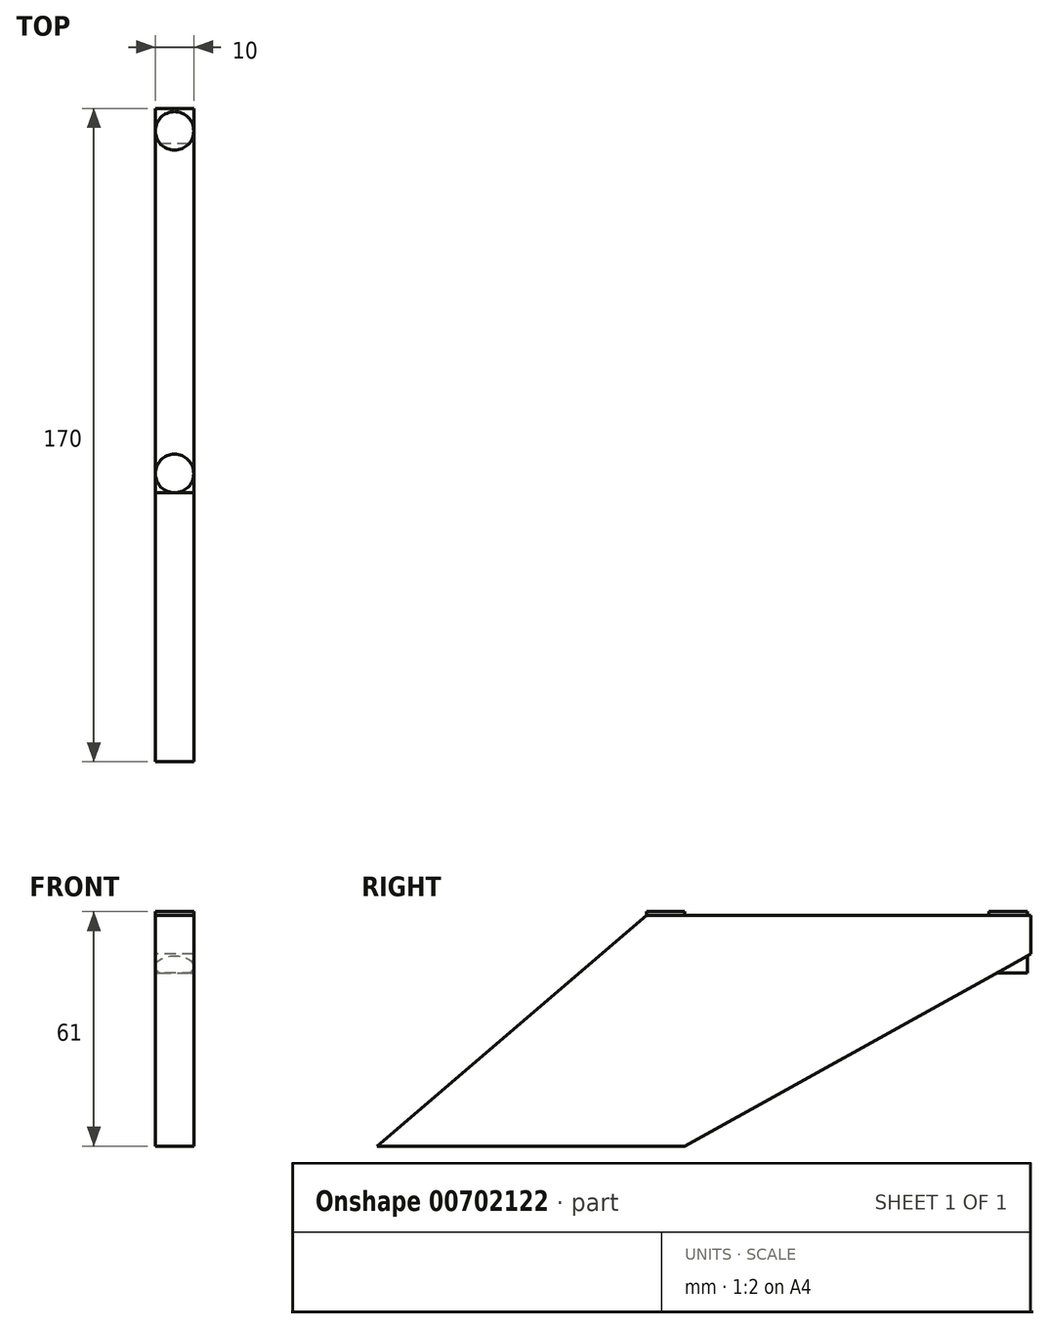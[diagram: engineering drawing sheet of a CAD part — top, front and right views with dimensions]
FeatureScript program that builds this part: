
annotation { "Feature Type Name" : "Feature", "Feature Type Description" : "" }
export const myFeature = defineFeature(function(context is Context, id is Id, definition is map)
    precondition{}
    {
        {
            var Q0;
            Q0=qCreatedBy(makeId("Right.planeOp"),FACE);
            var sketch = newSketch(context, id + "F0", { "sketchPlane" : qUnion([Q0])});
            skLineSegment(sketch, "E0", {"start": v(-41.23, -36.86) * mm, "end": v(-41.23, 23.14) * mm});
            skLineSegment(sketch, "E1", {"start": v(-41.23, 23.14) * mm, "end": v(58.77, 23.14) * mm});
            skLineSegment(sketch, "E2", {"start": v(-41.23, -36.86) * mm, "end": v(-111.23, -36.86) * mm});
            skLineSegment(sketch, "E3", {"start": v(-111.23, -36.86) * mm, "end": v(-41.23, 23.14) * mm});
            skLineSegment(sketch, "E4", {"start": v(58.77, 23.14) * mm, "end": v(58.77, 13.14) * mm});
            skLineSegment(sketch, "E5", {"start": v(58.77, 13.14) * mm, "end": v(-31.23, -36.86) * mm});
            skLineSegment(sketch, "E6", {"start": v(-31.23, -36.86) * mm, "end": v(-41.23, -36.86) * mm});
            skSolve(sketch);
        }
        {
            var Q0;
            Q0=makeQuery(id+"F0.imprint","IMPRINT",FACE,{"disambiguationData":[TD([[makeQuery(id+"F0.imprint","IMPRINT",EDGE,{"derivedFrom":sQuery(id+"F0.wireOp",EDGE,"E0")}),1.0]])]});
            var Q1;
            Q1=makeQuery(id+"F0.imprint","IMPRINT",FACE,{"disambiguationData":[TD([[makeQuery(id+"F0.imprint","IMPRINT",EDGE,{"derivedFrom":sQuery(id+"F0.wireOp",EDGE,"E0")}),-1.0]])]});
            extrude(context, id + "F1", {"entities" : qUnion([Q0, Q1]), "endBound" : BoundingType.SYMMETRIC, "depth" : 10 * mm, "offsetDistance" : 25 * mm});
        }
        {
            var Q0;
            Q0=makeQuery(id+"F1.opExtrude","SWEPT_FACE",FACE,{"disambiguationData":[OSD([sQuery(id+"F0.wireOp",EDGE,"E1")])]});
            var sketch = newSketch(context, id + "F2", { "sketchPlane" : qUnion([Q0])});
            skCircle(sketch, "E7", {"center": v(0, 52.9) * mm, "radius": 5 * mm});
            skSolve(sketch);
        }
        {
            var Q0;
            {var subQ0=sQuery(id+"F2.wireOp",EDGE,"E7");var subQ1=sQuery(id+"F0.wireOp",EDGE,"E1");var subQ2=makeQuery(id+"F2.imprint","INTERSECT",VERTEX,{"derivedFrom":[makeQuery(id+"F1.opExtrude","CAP_EDGE",EDGE,{"disambiguationData":[OSD([subQ1])],"isStart":true}),subQ0]});Q0=makeQuery(id+"F2.imprint","IMPRINT",FACE,{"disambiguationData":[TD([[makeQuery(id+"F2.imprint","IMPRINT",EDGE,{"disambiguationData":[TD([[subQ2,1.0]])],"derivedFrom":subQ0}),1.0]])]});}
            extrude(context, id + "F3", {"entities" : qUnion([Q0]), "operationType" : NewBodyOperationType.ADD, "depth" : 1 * mm, "offsetDistance" : 25 * mm, "hasSecondDirection" : true, "secondDirectionOppositeDirection" : true, "secondDirectionDepth" : 15 * mm});
        }
        {
            var Q0;
            {var subQ0=sQuery(id+"F0.wireOp",EDGE,"E3");var subQ5=sQuery(id+"F0.wireOp",EDGE,"E1");var subQ6=makeQuery(id+"F1.opExtrude","SWEPT_FACE",FACE,{"disambiguationData":[OSD([subQ5])]});Q0=makeQuery(id+"F3.boolean.opBoolean","SPLIT",FACE,{"disambiguationData":[TD([makeQuery(id+"F1.opExtrude","SWEPT_FACE",FACE,{"disambiguationData":[OSD([subQ0])]})])],"derivedFrom":subQ6});}
            var sketch = newSketch(context, id + "F4", { "sketchPlane" : qUnion([Q0])});
            skCircle(sketch, "E8", {"center": v(0, -36.23) * mm, "radius": 5 * mm});
            skSolve(sketch);
        }
        {
            var Q0;
            {var subQ0=sQuery(id+"F4.wireOp",EDGE,"E8");var subQ1=sQuery(id+"F0.wireOp",EDGE,"E1");var subQ6=sQuery(id+"F0.wireOp",EDGE,"E3");var subQ12=makeQuery(id+"F4.imprint","INTERSECT",VERTEX,{"derivedFrom":[makeQuery(id+"F1.opExtrude","SWEPT_EDGE",EDGE,{"disambiguationData":[OSD([sQuery(id+"F0.wireOp",EDGE,"E0"),subQ1,subQ6])]}),subQ0]});Q0=makeQuery(id+"F4.imprint","IMPRINT",FACE,{"disambiguationData":[TD([[makeQuery(id+"F4.imprint","IMPRINT",EDGE,{"disambiguationData":[TD([[subQ12,1.0]])],"derivedFrom":subQ0}),1.0]])]});}
            extrude(context, id + "F5", {"entities" : qUnion([Q0]), "operationType" : NewBodyOperationType.ADD, "depth" : 1 * mm, "offsetDistance" : 25 * mm, "hasSecondDirection" : true, "secondDirectionOppositeDirection" : true, "secondDirectionDepth" : 59.9 * mm});
        }
    });
